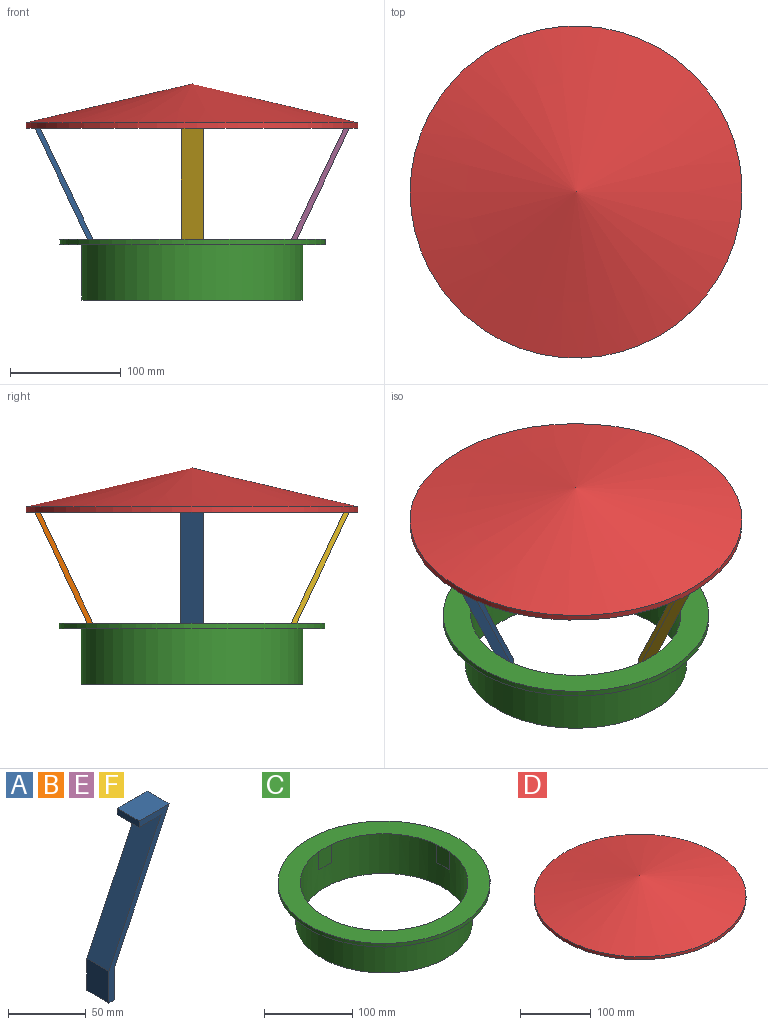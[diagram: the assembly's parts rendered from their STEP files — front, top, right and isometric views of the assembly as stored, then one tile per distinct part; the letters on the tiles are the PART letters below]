
ASSEMBLY  parts=6 mates=5
PART A: 10 faces, bbox 55x20x130 mm
  f0: plane 25x20mm, normal (-1,0,0), area 500mm2, adj f1,f7,f8,f9
  f1: plane 20x5mm, normal (0,0,-1), area 100mm2, adj f0,f2,f8,f9
  f2: plane 25x20mm, normal (1,0,0), area 500mm2, adj f1,f3,f8,f9
  f3: plane 105x50mm, normal (0.9,0,-0.43), area 2325.9mm2, adj f2,f4,f8,f9
  f4: plane 27.38x20mm, normal (0,0,1), area 547.6mm2, adj f3,f5,f8,f9
  f5: plane 20x5mm, normal (-1,0,0), area 100mm2, adj f4,f6,f8,f9
  f6: plane 20x20mm, normal (0,0,-1), area 400mm2, adj f5,f7,f8,f9
  f7: plane 100x47.62mm, normal (-0.9,0,0.43), area 2215.2mm2, adj f0,f6,f8,f9
  f8: plane 130x55mm, normal (0,-1,0), area 756mm2, adj f0,f1,f2,f3,f4,f5,f6,f7
  f9: plane 130x55mm, normal (0,1,0), area 756mm2, adj f0,f1,f2,f3,f4,f5,f6,f7
PART B: same geometry as A
PART C: 14 faces, bbox 240x240x55 mm
  f0: cylinder r=95mm len=190mm, axis (0,0,-1), area 30825.9mm2, adj f2,f4,f6,f7,f8,f9,f10,f11
  f1: cylinder r=100mm len=200mm, axis (0,0,-1), area 31415.9mm2, adj f2,f5
  f2: plane 200x200mm, normal (0,0,-1), area 3063.1mm2, adj f0,f1
  f3: cylinder r=120mm len=240mm, axis (0,0,-1), area 3769.9mm2, adj f4,f5
  f4: plane 240x240mm, normal (0,0,1), area 16914.2mm2, adj f0,f3,f7,f9,f11,f13
  f5: plane 240x240mm, normal (0,0,-1), area 13823mm2, adj f1,f3
  f6: plane 20x0.53mm, normal (0,0,-1), area 7mm2, adj f0,f7
  f7: plane 25x20mm, normal (0,-1,0), area 500mm2, adj f0,f4,f6
  f8: plane 20x0.53mm, normal (0,0,-1), area 7mm2, adj f0,f9
  f9: plane 25x20mm, normal (-1,0,0), area 500mm2, adj f0,f4,f8
  f10: plane 20x0.53mm, normal (0,0,-1), area 7mm2, adj f0,f11
  f11: plane 25x20mm, normal (0,1,0), area 500mm2, adj f0,f4,f10
  f12: plane 20x0.53mm, normal (0,0,-1), area 7mm2, adj f0,f13
  f13: plane 25x20mm, normal (1,0,0), area 500mm2, adj f0,f4,f12
PART D: 3 faces, bbox 300x300x40.1 mm
  f0: cone r=0mm half-angle=76.9deg, axis (0,0,-1), area 72584.6mm2, adj f2
  f1: cone r=150mm half-angle=76.9deg, axis (0,0,-1), area 72584.6mm2, adj f2
  f2: cylinder r=150mm len=300mm, axis (0,0,-1), area 4839mm2, adj f0,f1
PART E: same geometry as A
PART F: same geometry as A
PLACE A rot(axis=(0,0,-1),180deg) t=(-108.38,-23.49,-1.36)mm
PLACE B rot(axis=(0,0,1),90deg) t=(-28.91,75.99,-1.36)mm
PLACE C t=(-18.91,-13.49,-31.36)mm fixed
PLACE D t=(-18.91,-13.49,158.64)mm
PLACE E t=(70.57,-3.49,-1.36)mm
PLACE F rot(axis=(0,0,-1),90deg) t=(-8.91,-102.96,-1.36)mm
MATE fastened F.f2 <-> C.f11  axis (0,-1,0) through (-18.91,-107.96,23.64)mm
MATE fastened B.f2 <-> C.f7  axis (0,1,0) through (-18.91,80.99,23.64)mm
MATE fastened D.f0 <-> C.f0  axis (0,0,-1) through (-18.91,-13.49,123.64)mm
MATE fastened E.f2 <-> C.f9  axis (1,0,0) through (75.57,-13.49,23.64)mm
MATE fastened A.f2 <-> C.f13  axis (-1,0,0) through (-113.38,-13.49,23.64)mm
